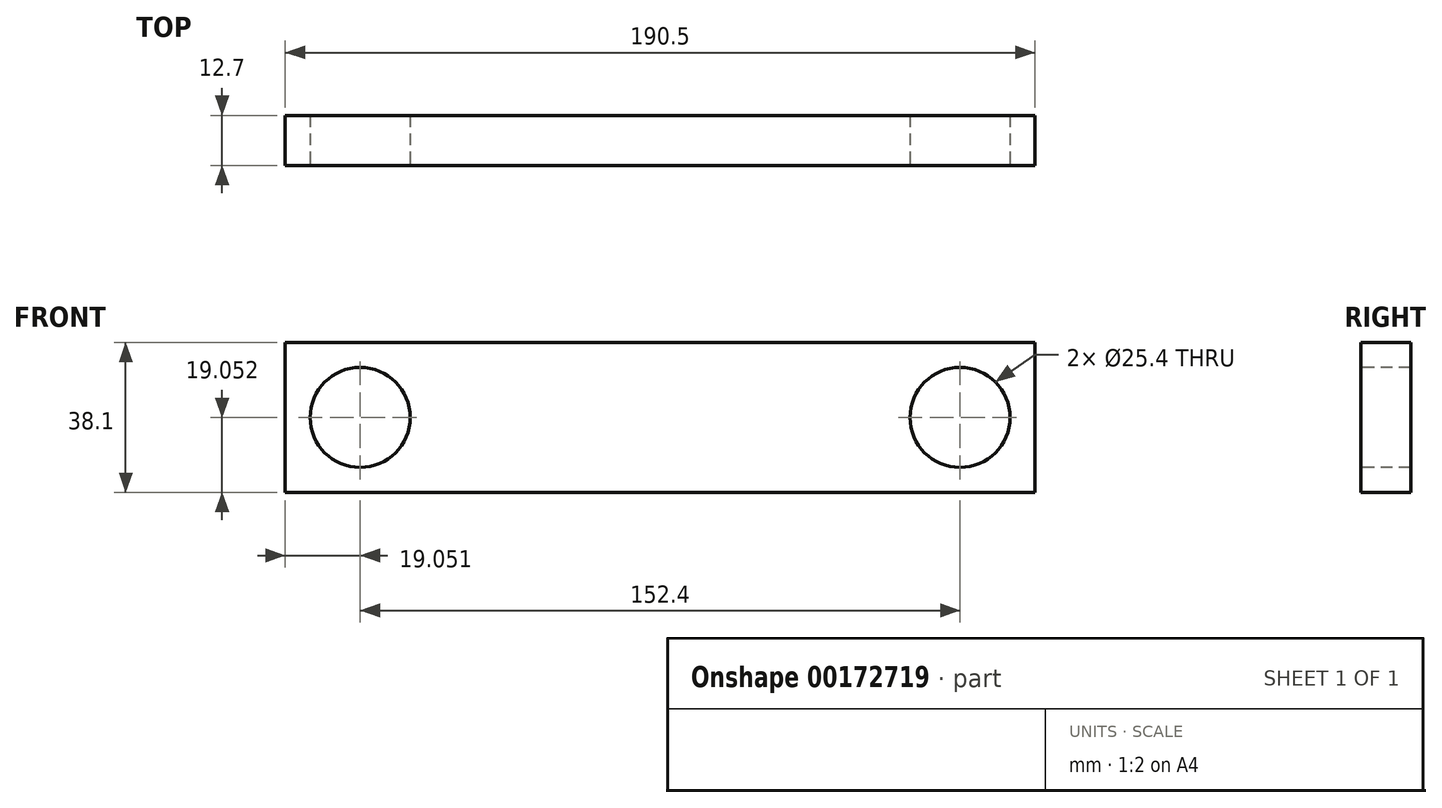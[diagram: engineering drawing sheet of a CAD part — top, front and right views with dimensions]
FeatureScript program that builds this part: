
annotation { "Feature Type Name" : "Feature", "Feature Type Description" : "" }
export const myFeature = defineFeature(function(context is Context, id is Id, definition is map)
    precondition{}
    {
        {
            var Q0;
            Q0=qCreatedBy(makeId("Front.planeOp"),FACE);
            var sketch = newSketch(context, id + "F0", { "sketchPlane" : qUnion([Q0])});
            skLineSegment(sketch, "E0.bottom", {"start": v(-88.96, 25.47) * mm, "end": v(101.54, 25.47) * mm});
            skLineSegment(sketch, "E0.top", {"start": v(-88.96, -12.63) * mm, "end": v(101.54, -12.63) * mm});
            skLineSegment(sketch, "E0.left", {"start": v(-88.96, 25.47) * mm, "end": v(-88.96, -12.63) * mm});
            skLineSegment(sketch, "E0.right", {"start": v(101.54, 25.47) * mm, "end": v(101.54, -12.63) * mm});
            skSolve(sketch);
        }
        {
            var Q0;
            Q0 = qSketchRegion(id + "F0", true);
            extrude(context, id + "F1", {"entities" : qUnion([Q0]), "depth" : 12.7 * mm});
        }
        {
            var Q0;
            Q0=makeQuery(id+"F1.opExtrude","CAP_FACE",FACE,{"disambiguationData":[OSD([sQuery(id+"F0.wireOp",EDGE,"E0.bottom"),sQuery(id+"F0.wireOp",EDGE,"E0.top"),sQuery(id+"F0.wireOp",EDGE,"E0.left"),sQuery(id+"F0.wireOp",EDGE,"E0.right")])],"isStart":false});
            var sketch = newSketch(context, id + "F2", { "sketchPlane" : qUnion([Q0])});
            skCircle(sketch, "E1", {"center": v(-69.9, 6.42) * mm, "radius": 12.7 * mm});
            skPoint(sketch, "E1.centerSnap0", {"position": v(-88.96, 6.42) * mm});
            skCircle(sketch, "E2", {"center": v(82.5, 6.42) * mm, "radius": 12.7 * mm});
            skPoint(sketch, "E2.centerSnap0", {"position": v(101.54, 6.42) * mm});
            skSolve(sketch);
        }
        {
            var Q0;
            Q0=sQuery(id+"F2.wireOp",VERTEX,"E1.center");
            var Q1;
            Q1=sQuery(id+"F2.wireOp",VERTEX,"E2.center");
            var Q2;
            Q2=makeQuery(id+"F1.opExtrude","SWEPT_BODY",BODY,{"disambiguationData":[OSD([sQuery(id+"F0.wireOp",EDGE,"E0.bottom"),sQuery(id+"F0.wireOp",EDGE,"E0.top"),sQuery(id+"F0.wireOp",EDGE,"E0.left"),sQuery(id+"F0.wireOp",EDGE,"E0.right")])]});
            hole(context, id + "F3", {"style" : HoleStyle.SIMPLE, "endStyle" : HoleEndStyle.THROUGH, "holeDiameter" : 25.4 * mm, "locations" : qUnion([Q0, Q1]), "scope" : qUnion([Q2]), "isTappedThrough" : true});
        }
    });
